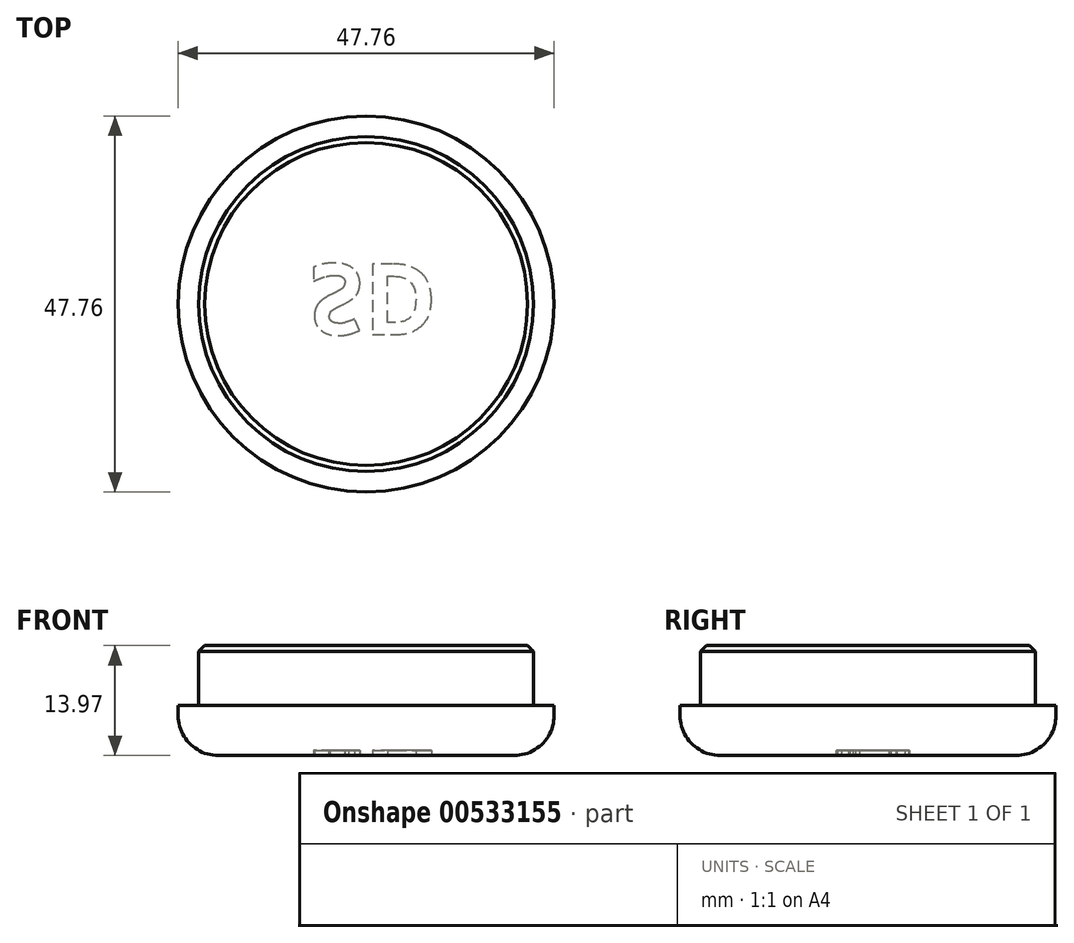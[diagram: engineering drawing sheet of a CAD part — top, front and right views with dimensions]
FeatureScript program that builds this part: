
annotation { "Feature Type Name" : "Feature", "Feature Type Description" : "" }
export const myFeature = defineFeature(function(context is Context, id is Id, definition is map)
    precondition{}
    {
        {
            var Q0;
            Q0=qCreatedBy(makeId("Top.planeOp"),FACE);
            var sketch = newSketch(context, id + "F0", { "sketchPlane" : qUnion([Q0])});
            skCircle(sketch, "E0", {"center": v(0, 0) * mm, "radius": 23.88 * mm});
            skSolve(sketch);
        }
        {
            var Q0;
            Q0=makeQuery(id+"F0.imprint","IMPRINT",FACE,{"disambiguationData":[TD([[makeQuery(id+"F0.imprint","IMPRINT",EDGE,{"derivedFrom":sQuery(id+"F0.wireOp",EDGE,"E0")}),1.0]])]});
            extrude(context, id + "F1", {"entities" : qUnion([Q0]), "depth" : 6.35 * mm, "offsetDistance" : 25.4 * mm});
        }
        {
            var Q0;
            Q0=makeQuery(id+"F1.opExtrude","CAP_FACE",FACE,{"disambiguationData":[OSD([sQuery(id+"F0.wireOp",EDGE,"E0")])],"isStart":false});
            var sketch = newSketch(context, id + "F2", { "sketchPlane" : qUnion([Q0])});
            skCircle(sketch, "E1", {"center": v(0, 0) * mm, "radius": 21.27 * mm});
            skSolve(sketch);
        }
        {
            var Q0;
            Q0=makeQuery(id+"F2.imprint","IMPRINT",FACE,{"disambiguationData":[TD([[makeQuery(id+"F2.imprint","IMPRINT",EDGE,{"derivedFrom":sQuery(id+"F2.wireOp",EDGE,"E1")}),1.0]])]});
            extrude(context, id + "F3", {"entities" : qUnion([Q0]), "operationType" : NewBodyOperationType.ADD, "depth" : 7.62 * mm, "offsetDistance" : 25.4 * mm});
        }
        {
            var Q0;
            Q0=makeQuery(id+"F1.opExtrude","CAP_EDGE",EDGE,{"disambiguationData":[OSD([sQuery(id+"F0.wireOp",EDGE,"E0")])],"isStart":true});
            fillet(context, id + "F4", {"entities" : qUnion([Q0]), "radius" : 5.08 * mm, "tangentPropagation" : true, "allowEdgeOverflow" : false});
        }
        {
            var Q0;
            Q0=makeQuery(id+"F1.opExtrude","CAP_FACE",FACE,{"disambiguationData":[OSD([sQuery(id+"F0.wireOp",EDGE,"E0")])],"isStart":true});
            var sketch = newSketch(context, id + "F5", { "sketchPlane" : qUnion([Q0])});
            skText(sketch, "E2", { "text": "SD", "fontName": "OpenSans-Bold.ttf"});
            const initialGuessF5  = {"E2": [-0.00724, -0.0051, 1, 0, 0.00907]};
            skSetInitialGuess(sketch, initialGuessF5);
            skSolve(sketch);
        }
        {
            var Q0;
            Q0 = qSketchRegion(id + "F5", true);
            extrude(context, id + "F6", {"entities" : qUnion([Q0]), "operationType" : NewBodyOperationType.REMOVE, "oppositeDirection" : true, "depth" : 0.64 * mm, "offsetDistance" : 25.4 * mm});
        }
        {
            var Q0;
            Q0=makeQuery(id+"F3.opExtrude","CAP_EDGE",EDGE,{"disambiguationData":[OSD([sQuery(id+"F2.wireOp",EDGE,"E1")])],"isStart":false});
            chamfer(context, id + "F7", {"entities" : qUnion([Q0]), "width" : 0.76 * mm, "tangentPropagation" : true});
        }
    });
